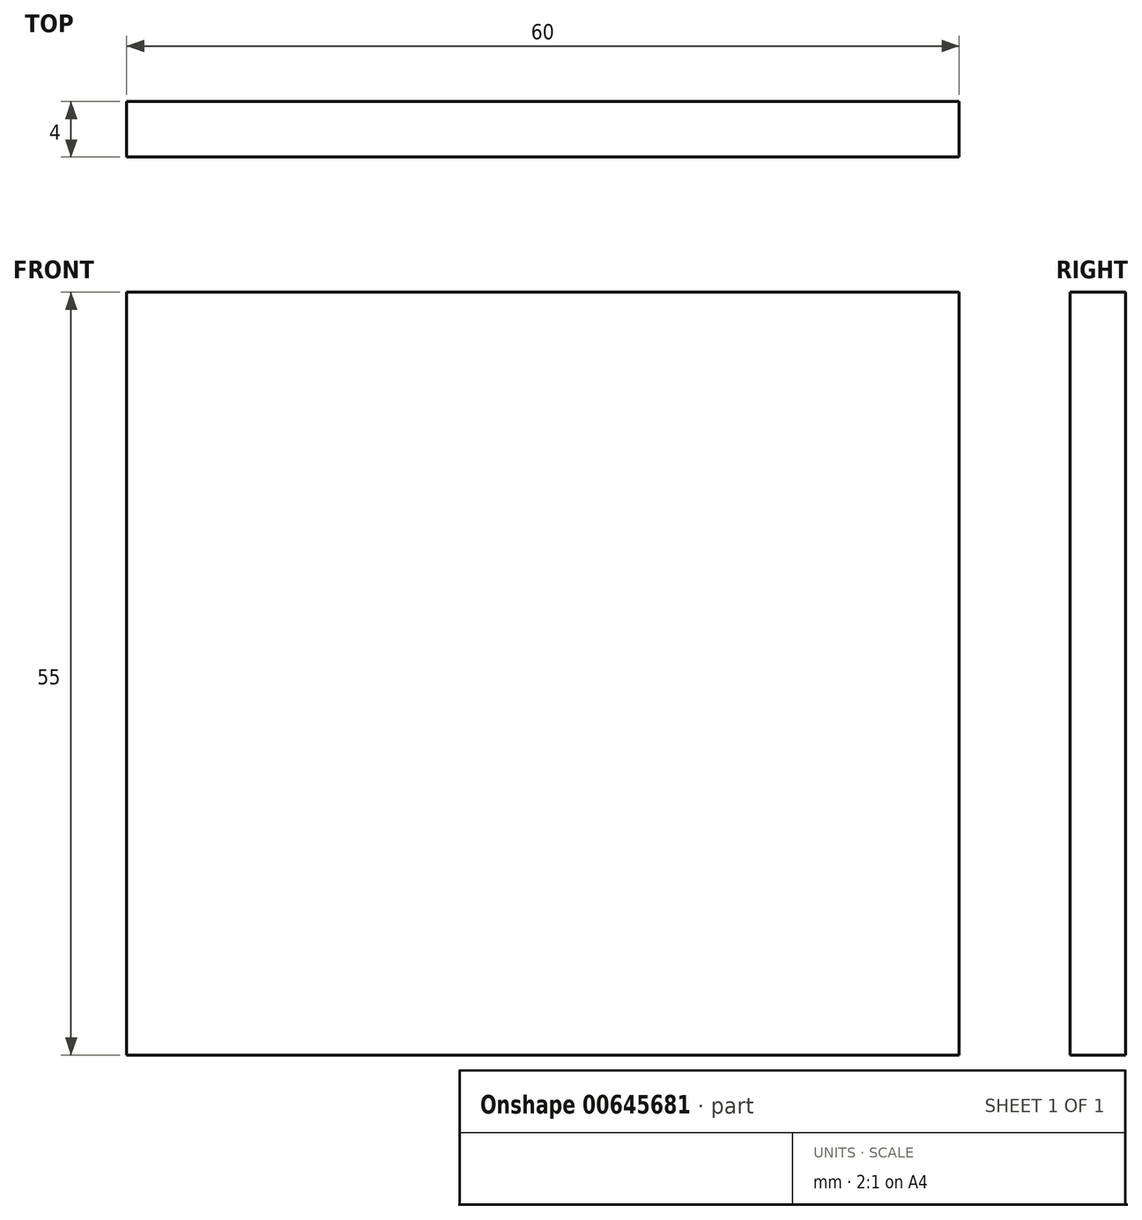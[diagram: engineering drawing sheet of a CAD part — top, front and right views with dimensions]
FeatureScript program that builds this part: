
annotation { "Feature Type Name" : "Feature", "Feature Type Description" : "" }
export const myFeature = defineFeature(function(context is Context, id is Id, definition is map)
    precondition{}
    {
        {
            var Q0;
            Q0=qCreatedBy(makeId("Front.planeOp"),FACE);
            var sketch = newSketch(context, id + "F0", { "sketchPlane" : qUnion([Q0])});
            skLineSegment(sketch, "E0.bottom", {"start": v(-27.1, 55) * mm, "end": v(32.9, 55) * mm});
            skLineSegment(sketch, "E0.top", {"start": v(-27.1, 0) * mm, "end": v(32.9, 0) * mm});
            skLineSegment(sketch, "E0.left", {"start": v(-27.1, 55) * mm, "end": v(-27.1, 0) * mm});
            skLineSegment(sketch, "E0.right", {"start": v(32.9, 55) * mm, "end": v(32.9, 0) * mm});
            skSolve(sketch);
        }
        {
            var Q0;
            Q0 = qSketchRegion(id + "F0", true);
            extrude(context, id + "F1", {"entities" : qUnion([Q0]), "depth" : 4 * mm, "offsetDistance" : 25 * mm});
        }
    });
